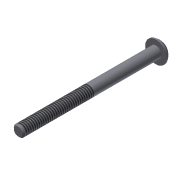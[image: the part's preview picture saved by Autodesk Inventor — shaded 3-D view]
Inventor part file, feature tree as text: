
AUTODESK INVENTOR PART (.ipt)
format: ipt  version: 2013 (Build 170138000, 138)  size: 118,784 bytes
history: native  units: in
note: dims shown in document units (in); Inventor stores cm internally (conversion verified against a paired STEP export)
features: sketch x3, extrude x2, revolve x1, chamfer x1, thread x1
ambient origin geometry x8: Origin, YZ Plane, XZ Plane, XY Plane, X Axis, Y Axis, Z Axis, Center Point
bodies: Solid1 (feature_tree)
feature tree (8):
  extrude  "Extrusion1"  Depth=2.0in TaperAngle=0.0deg
  revolve  "Revolution1"  [1 undecoded]
  extrude  "Extrusion2"  Depth=0.0938in
  chamfer  "Chamfer1"  Distance=0.0625in
  thread  "Thread1"  [1 undecoded]
  sketch  "Sketch1"  dims[d0=0.164in d1=2.0in d2=0.0in]
  sketch  "Sketch2"  dims[d3=0.087in d6=0.08in]
  sketch  "Sketch3"  dims[d7=90.0deg d8=0.0938in d9=0.0625in d10=0.0in d13=0.02in d14=0.125in d15=45.0deg d16=1.0in d17=0.0in d19=0.156in]
note: 2 required parameter values undecoded (feature->parameter linkage not recoverable at this tier; creation-order binding heuristic only, values carry confidence <= 0.55)